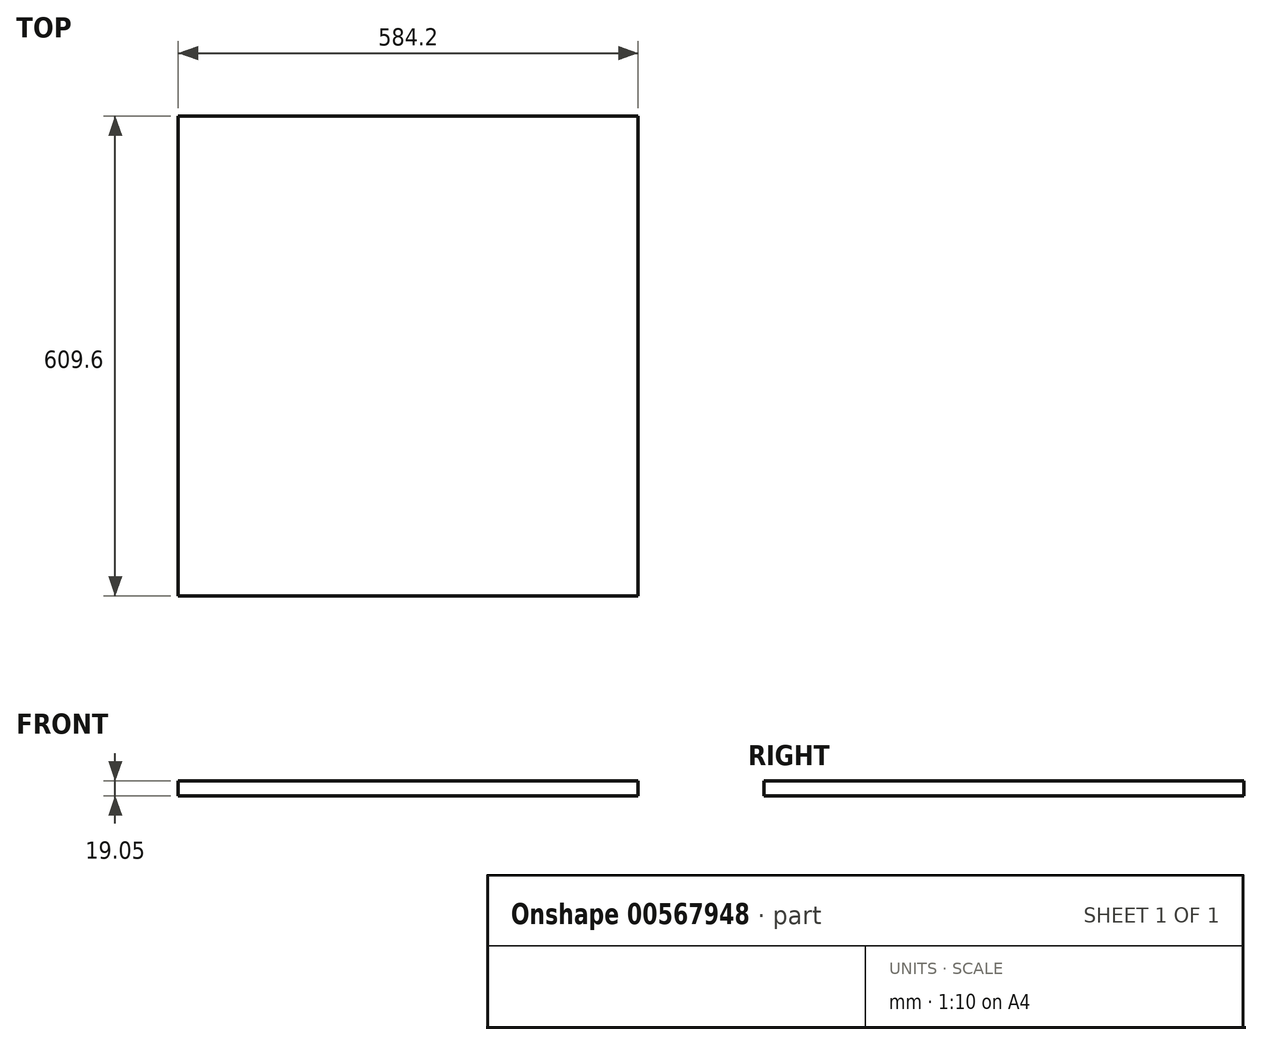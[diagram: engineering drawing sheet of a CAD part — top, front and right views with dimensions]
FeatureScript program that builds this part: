
annotation { "Feature Type Name" : "Feature", "Feature Type Description" : "" }
export const myFeature = defineFeature(function(context is Context, id is Id, definition is map)
    precondition{}
    {
        {
            var Q0;
            Q0=qCreatedBy(makeId("Top.planeOp"),FACE);
            var sketch = newSketch(context, id + "F0", { "sketchPlane" : qUnion([Q0])});
            skLineSegment(sketch, "E0.bottom", {"start": v(0, 0) * mm, "end": v(584.2, 0) * mm});
            skLineSegment(sketch, "E0.top", {"start": v(0, 609.6) * mm, "end": v(584.2, 609.6) * mm});
            skLineSegment(sketch, "E0.left", {"start": v(0, 0) * mm, "end": v(0, 609.6) * mm});
            skLineSegment(sketch, "E0.right", {"start": v(584.2, 0) * mm, "end": v(584.2, 609.6) * mm});
            skSolve(sketch);
        }
        {
            var Q0;
            Q0 = qSketchRegion(id + "F0", true);
            extrude(context, id + "F1", {"entities" : qUnion([Q0]), "depth" : 19.05 * mm, "offsetDistance" : 25.4 * mm});
        }
    });
